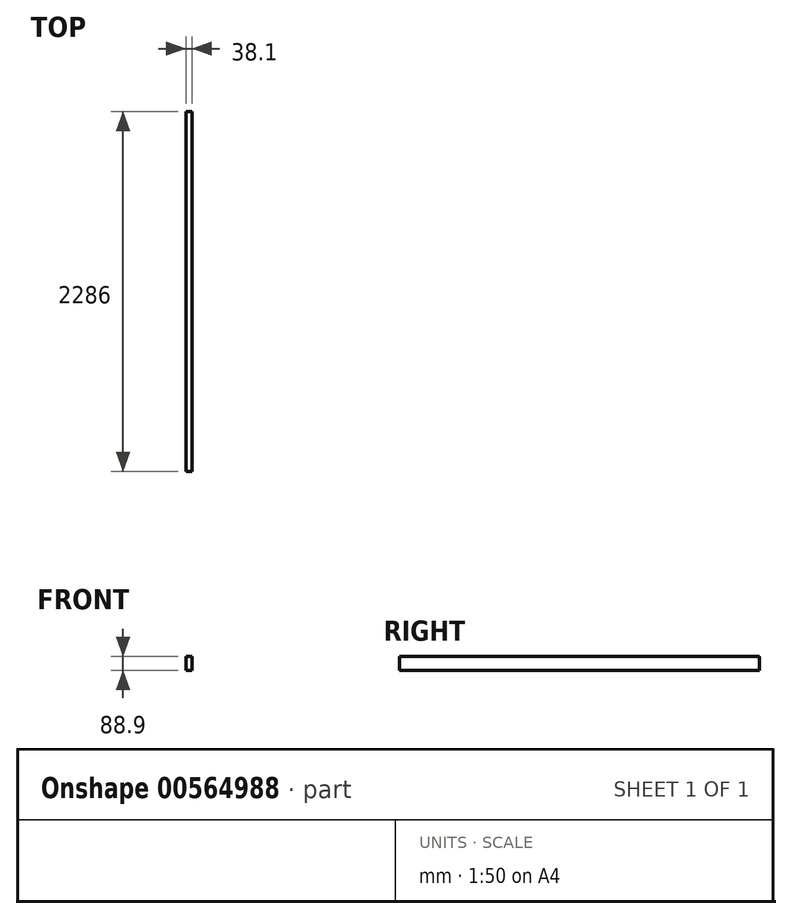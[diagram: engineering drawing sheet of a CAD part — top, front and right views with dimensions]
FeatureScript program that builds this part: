
annotation { "Feature Type Name" : "Feature", "Feature Type Description" : "" }
export const myFeature = defineFeature(function(context is Context, id is Id, definition is map)
    precondition{}
    {
        {
            var Q0;
            Q0=qCreatedBy(makeId("Front.planeOp"),FACE);
            var sketch = newSketch(context, id + "F0", { "sketchPlane" : qUnion([Q0])});
            skLineSegment(sketch, "E0.bottom", {"start": v(0, 0) * mm, "end": v(38.1, 0) * mm});
            skLineSegment(sketch, "E0.top", {"start": v(0, 88.9) * mm, "end": v(38.1, 88.9) * mm});
            skLineSegment(sketch, "E0.left", {"start": v(0, 0) * mm, "end": v(0, 88.9) * mm});
            skLineSegment(sketch, "E0.right", {"start": v(38.1, 0) * mm, "end": v(38.1, 88.9) * mm});
            skSolve(sketch);
        }
        {
            var Q0;
            Q0 = qSketchRegion(id + "F0", true);
            extrude(context, id + "F1", {"entities" : qUnion([Q0]), "depth" : 2286 * mm, "offsetDistance" : 25.4 * mm});
        }
    });
